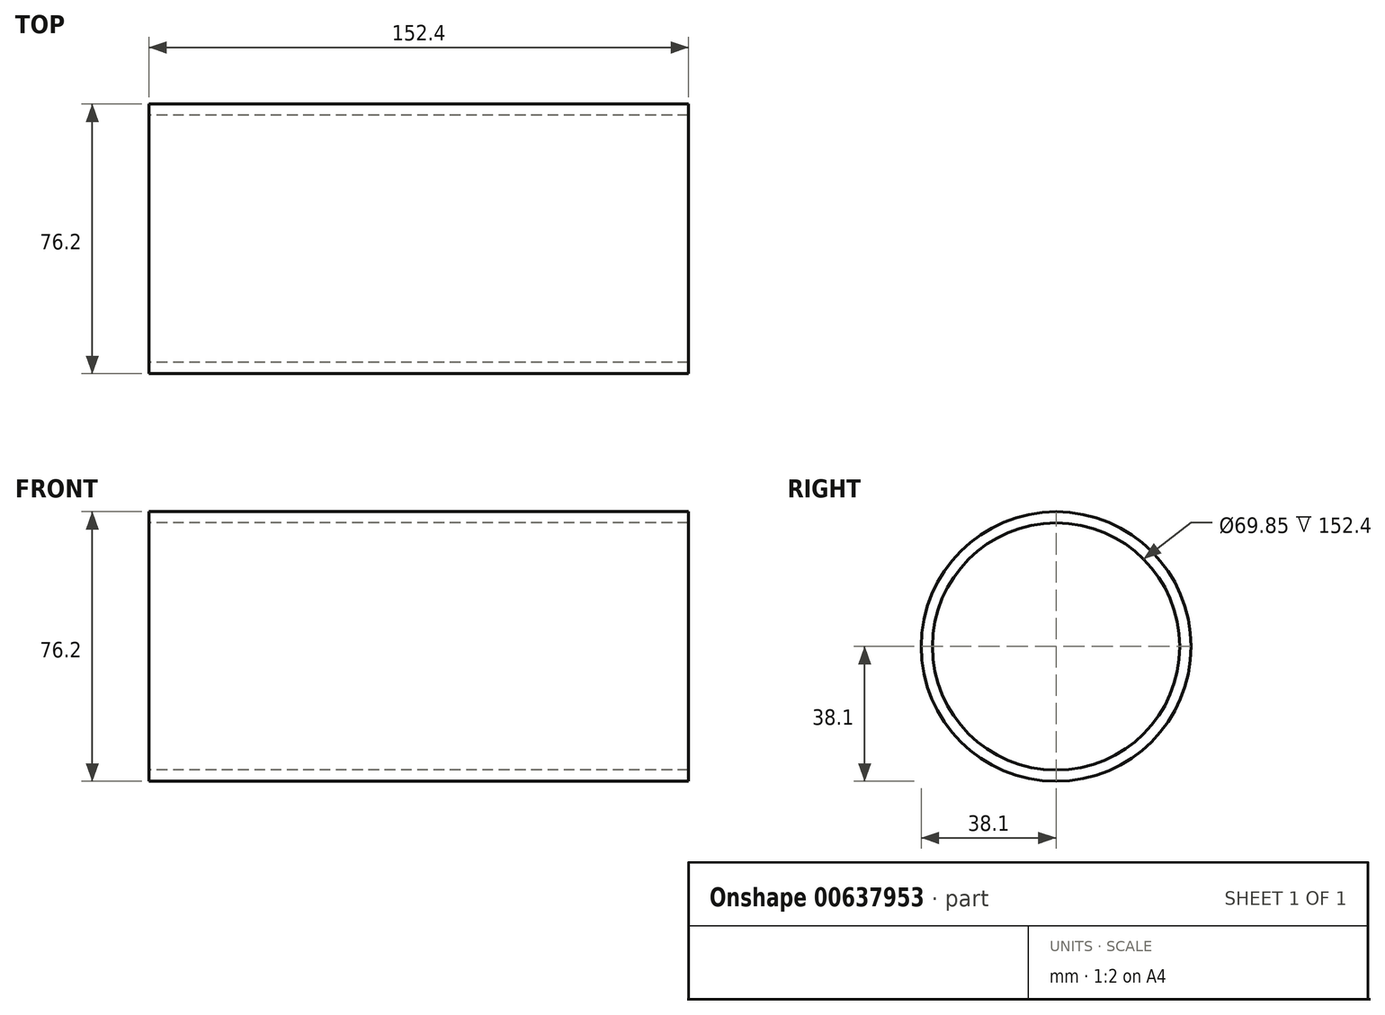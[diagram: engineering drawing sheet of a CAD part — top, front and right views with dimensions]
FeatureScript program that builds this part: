
annotation { "Feature Type Name" : "Feature", "Feature Type Description" : "" }
export const myFeature = defineFeature(function(context is Context, id is Id, definition is map)
    precondition{}
    {
        {
            var Q0;
            Q0=qCreatedBy(makeId("Right.planeOp"),FACE);
            var sketch = newSketch(context, id + "F0", { "sketchPlane" : qUnion([Q0])});
            skCircle(sketch, "E0", {"center": v(0, 0) * mm, "radius": 38.1 * mm});
            skCircle(sketch, "E1", {"center": v(0, 0) * mm, "radius": 34.93 * mm});
            skSolve(sketch);
        }
        {
            var Q0;
            Q0=makeQuery(id+"F0.imprint","IMPRINT",FACE,{"disambiguationData":[TD([[makeQuery(id+"F0.imprint","IMPRINT",EDGE,{"derivedFrom":sQuery(id+"F0.wireOp",EDGE,"E0")}),1.0]])]});
            extrude(context, id + "F1", {"entities" : qUnion([Q0]), "depth" : 152.4 * mm, "offsetDistance" : 25.4 * mm});
        }
    });
